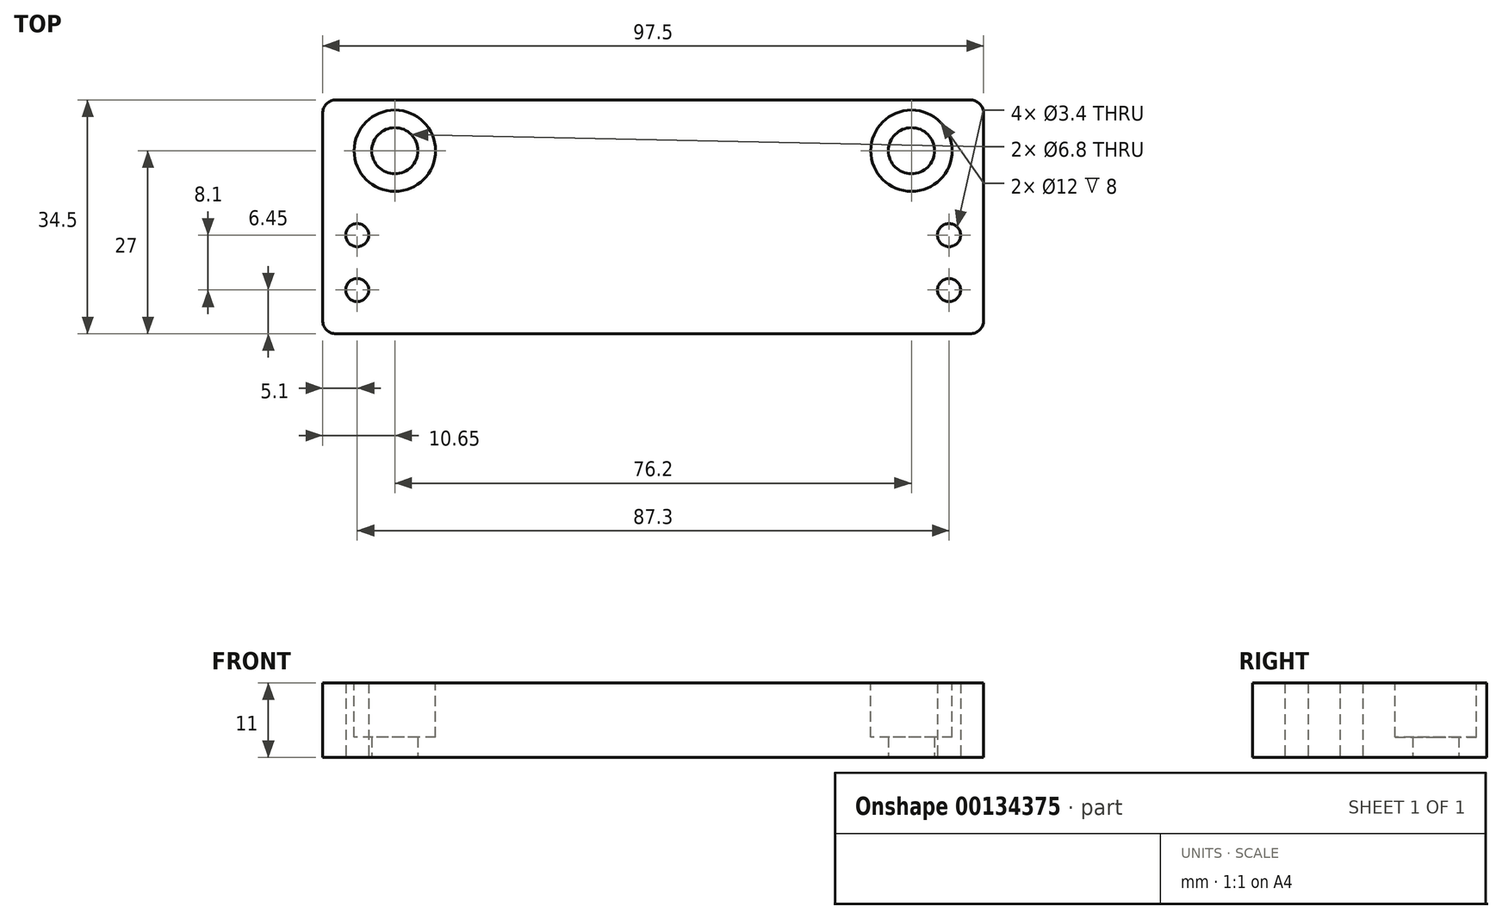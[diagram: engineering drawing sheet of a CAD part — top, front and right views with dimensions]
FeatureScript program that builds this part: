
annotation { "Feature Type Name" : "Feature", "Feature Type Description" : "" }
export const myFeature = defineFeature(function(context is Context, id is Id, definition is map)
    precondition{}
    {
        {
            var Q0;
            Q0=qCreatedBy(makeId("Top.planeOp"),FACE);
            var sketch = newSketch(context, id + "F0", { "sketchPlane" : qUnion([Q0])});
            skLineSegment(sketch, "E0.bottom", {"start": v(-48.75, 24) * mm, "end": v(48.75, 24) * mm});
            skLineSegment(sketch, "E1.bottom", {"start": v(-43.65, 4.05) * mm, "end": v(43.65, 4.05) * mm, "construction": true});
            skLineSegment(sketch, "E1.top", {"start": v(-43.65, -4.05) * mm, "end": v(43.65, -4.05) * mm, "construction": true});
            skLineSegment(sketch, "E1.left", {"start": v(-43.65, 4.05) * mm, "end": v(-43.65, -4.05) * mm, "construction": true});
            skLineSegment(sketch, "E1.right", {"start": v(43.65, 4.05) * mm, "end": v(43.65, -4.05) * mm, "construction": true});
            skCircle(sketch, "E2", {"center": v(-43.65, 4.05) * mm, "radius": 1.7 * mm});
            skCircle(sketch, "E3", {"center": v(-43.65, -4.05) * mm, "radius": 1.7 * mm});
            skCircle(sketch, "E4", {"center": v(43.65, 4.05) * mm, "radius": 1.7 * mm});
            skCircle(sketch, "E5", {"center": v(43.65, -4.05) * mm, "radius": 1.7 * mm});
            skCircle(sketch, "E6", {"center": v(38.1, 16.5) * mm, "radius": 3.4 * mm});
            skCircle(sketch, "E7", {"center": v(-38.1, 16.5) * mm, "radius": 3.4 * mm});
            skLineSegment(sketch, "E8", {"start": v(-48.75, 24) * mm, "end": v(-48.75, -10.5) * mm});
            skLineSegment(sketch, "E9", {"start": v(-48.75, -10.5) * mm, "end": v(48.75, -10.5) * mm});
            skLineSegment(sketch, "E10", {"start": v(48.75, -10.5) * mm, "end": v(48.75, 24) * mm});
            skSolve(sketch);
        }
        {
            var Q0;
            Q0 = qSketchRegion(id + "F0", true);
            extrude(context, id + "F1", {"entities" : qUnion([Q0]), "depth" : 11 * mm});
        }
        {
            var Q0;
            Q0=makeQuery(id+"F1.opExtrude","CAP_FACE",FACE,{"disambiguationData":[OSD([sQuery(id+"F0.wireOp",EDGE,"E0.bottom"),sQuery(id+"F0.wireOp",EDGE,"E2"),sQuery(id+"F0.wireOp",EDGE,"E3"),sQuery(id+"F0.wireOp",EDGE,"E4"),sQuery(id+"F0.wireOp",EDGE,"E5"),sQuery(id+"F0.wireOp",EDGE,"E6"),sQuery(id+"F0.wireOp",EDGE,"E7"),sQuery(id+"F0.wireOp",EDGE,"E8"),sQuery(id+"F0.wireOp",EDGE,"E9"),sQuery(id+"F0.wireOp",EDGE,"E10")])],"isStart":false});
            var sketch = newSketch(context, id + "F2", { "sketchPlane" : qUnion([Q0])});
            skCircle(sketch, "E11", {"center": v(-38.1, 16.5) * mm, "radius": 6 * mm});
            skCircle(sketch, "E12", {"center": v(38.1, 16.5) * mm, "radius": 6 * mm});
            skSolve(sketch);
        }
        {
            var Q0;
            Q0 = qSketchRegion(id + "F2", true);
            extrude(context, id + "F3", {"entities" : qUnion([Q0]), "operationType" : NewBodyOperationType.REMOVE, "oppositeDirection" : true, "depth" : 8 * mm});
        }
        {
            var Q0;
            Q0=makeQuery(id+"F1.opExtrude","SWEPT_EDGE",EDGE,{"disambiguationData":[OSD([sQuery(id+"F0.wireOp",EDGE,"E8"),sQuery(id+"F0.wireOp",EDGE,"E9")])]});
            var Q1;
            Q1=makeQuery(id+"F1.opExtrude","SWEPT_EDGE",EDGE,{"disambiguationData":[OSD([sQuery(id+"F0.wireOp",EDGE,"E0.bottom"),sQuery(id+"F0.wireOp",EDGE,"E8")])]});
            var Q2;
            Q2=makeQuery(id+"F1.opExtrude","SWEPT_EDGE",EDGE,{"disambiguationData":[OSD([sQuery(id+"F0.wireOp",EDGE,"E9"),sQuery(id+"F0.wireOp",EDGE,"E10")])]});
            var Q3;
            Q3=makeQuery(id+"F1.opExtrude","SWEPT_EDGE",EDGE,{"disambiguationData":[OSD([sQuery(id+"F0.wireOp",EDGE,"E0.bottom"),sQuery(id+"F0.wireOp",EDGE,"E10")])]});
            fillet(context, id + "F4", {"entities" : qUnion([Q0, Q1, Q2, Q3]), "radius" : 2 * mm, "tangentPropagation" : true, "allowEdgeOverflow" : false});
        }
    });
